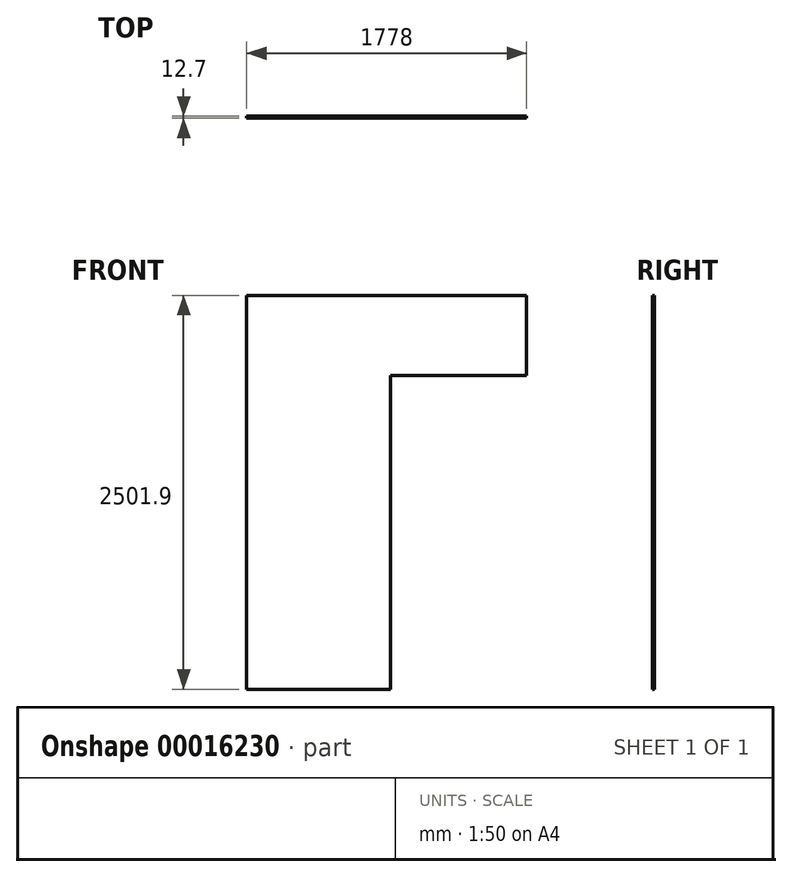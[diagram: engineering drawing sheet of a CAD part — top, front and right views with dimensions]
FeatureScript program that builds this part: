
annotation { "Feature Type Name" : "Feature", "Feature Type Description" : "" }
export const myFeature = defineFeature(function(context is Context, id is Id, definition is map)
    precondition{}
    {
        {
            var Q0;
            Q0=qCreatedBy(makeId("Front.planeOp"),FACE);
            var sketch = newSketch(context, id + "F0", { "sketchPlane" : qUnion([Q0])});
            skLineSegment(sketch, "E0", {"start": v(-719.42, 1729.48) * mm, "end": v(1058.58, 1729.48) * mm});
            skLineSegment(sketch, "E1", {"start": v(1058.58, 1729.48) * mm, "end": v(1058.58, 1221.48) * mm});
            skLineSegment(sketch, "E2", {"start": v(1058.58, 1221.48) * mm, "end": v(194.98, 1221.48) * mm});
            skLineSegment(sketch, "E3", {"start": v(194.98, 1221.48) * mm, "end": v(194.98, -772.42) * mm});
            skLineSegment(sketch, "E4", {"start": v(194.98, -772.42) * mm, "end": v(-719.42, -772.42) * mm});
            skLineSegment(sketch, "E5", {"start": v(-719.42, -772.42) * mm, "end": v(-719.42, 1729.48) * mm});
            skSolve(sketch);
        }
        {
            var Q0;
            Q0=makeQuery(id+"F0.imprint","IMPRINT",FACE,{"disambiguationData":[TD([[makeQuery(id+"F0.imprint","IMPRINT",EDGE,{"derivedFrom":sQuery(id+"F0.wireOp",EDGE,"E0")}),-1.0]])]});
            extrude(context, id + "F1", {"entities" : qUnion([Q0]), "oppositeDirection" : true, "depth" : 12.7 * mm});
        }
    });
